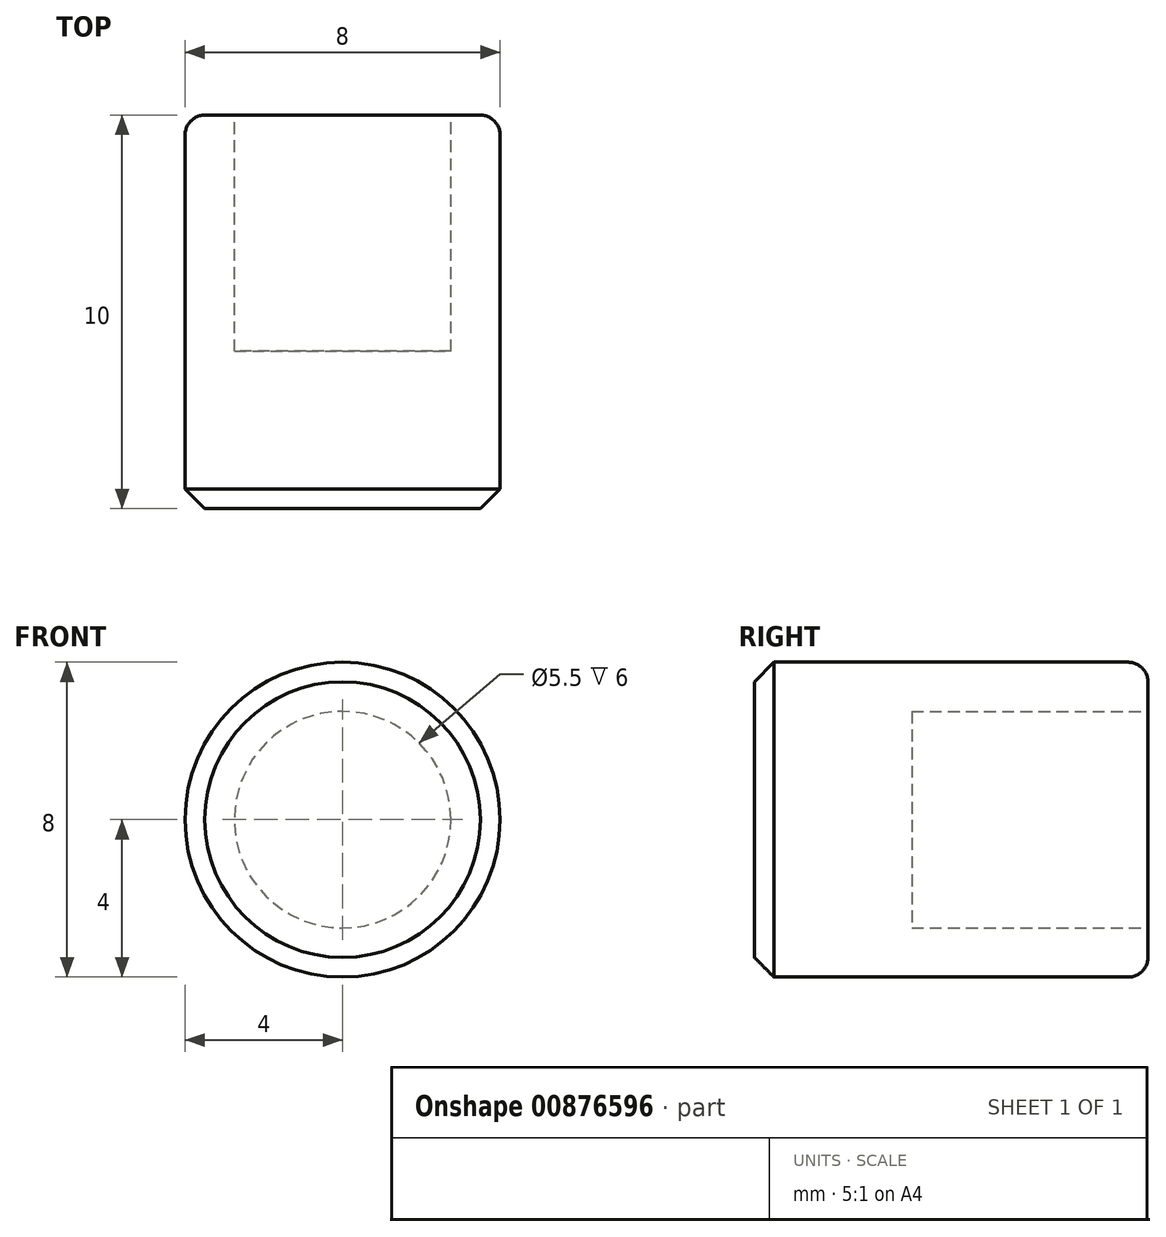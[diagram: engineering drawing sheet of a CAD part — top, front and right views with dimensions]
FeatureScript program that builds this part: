
annotation { "Feature Type Name" : "Feature", "Feature Type Description" : "" }
export const myFeature = defineFeature(function(context is Context, id is Id, definition is map)
    precondition{}
    {
        {
            var Q0;
            Q0=qCreatedBy(makeId("Front.planeOp"),FACE);
            var sketch = newSketch(context, id + "F0", { "sketchPlane" : qUnion([Q0])});
            skCircle(sketch, "E0", {"center": v(0, 0) * mm, "radius": 4 * mm});
            skSolve(sketch);
        }
        {
            var Q0;
            Q0=makeQuery(id+"F0.imprint","IMPRINT",FACE,{"disambiguationData":[TD([[makeQuery(id+"F0.imprint","IMPRINT",EDGE,{"derivedFrom":sQuery(id+"F0.wireOp",EDGE,"E0")}),1.0]])]});
            extrude(context, id + "F1", {"entities" : qUnion([Q0]), "depth" : 10 * mm, "offsetDistance" : 25 * mm});
        }
        {
            var Q0;
            Q0=makeQuery(id+"F1.opExtrude","CAP_FACE",FACE,{"disambiguationData":[OSD([sQuery(id+"F0.wireOp",EDGE,"E0")])],"isStart":false});
            chamfer(context, id + "F2", {"entities" : qUnion([Q0]), "width" : 0.5 * mm, "tangentPropagation" : true});
        }
        {
            var Q0;
            Q0=makeQuery(id+"F1.opExtrude","CAP_FACE",FACE,{"disambiguationData":[OSD([sQuery(id+"F0.wireOp",EDGE,"E0")])],"isStart":true});
            var sketch = newSketch(context, id + "F3", { "sketchPlane" : qUnion([Q0])});
            skCircle(sketch, "E1", {"center": v(0, 0) * mm, "radius": 2.75 * mm});
            skSolve(sketch);
        }
        {
            var Q0;
            Q0=makeQuery(id+"F3.imprint","IMPRINT",FACE,{"disambiguationData":[TD([[makeQuery(id+"F3.imprint","IMPRINT",EDGE,{"derivedFrom":sQuery(id+"F3.wireOp",EDGE,"E1")}),1.0]])]});
            extrude(context, id + "F4", {"entities" : qUnion([Q0]), "operationType" : NewBodyOperationType.REMOVE, "oppositeDirection" : true, "depth" : 6 * mm, "offsetDistance" : 25 * mm});
        }
        {
            var Q0;
            Q0=makeQuery(id+"F1.opExtrude","CAP_EDGE",EDGE,{"disambiguationData":[OSD([sQuery(id+"F0.wireOp",EDGE,"E0")])],"isStart":true});
            fillet(context, id + "F5", {"entities" : qUnion([Q0]), "radius" : 0.5 * mm, "tangentPropagation" : true, "allowEdgeOverflow" : false});
        }
    });
